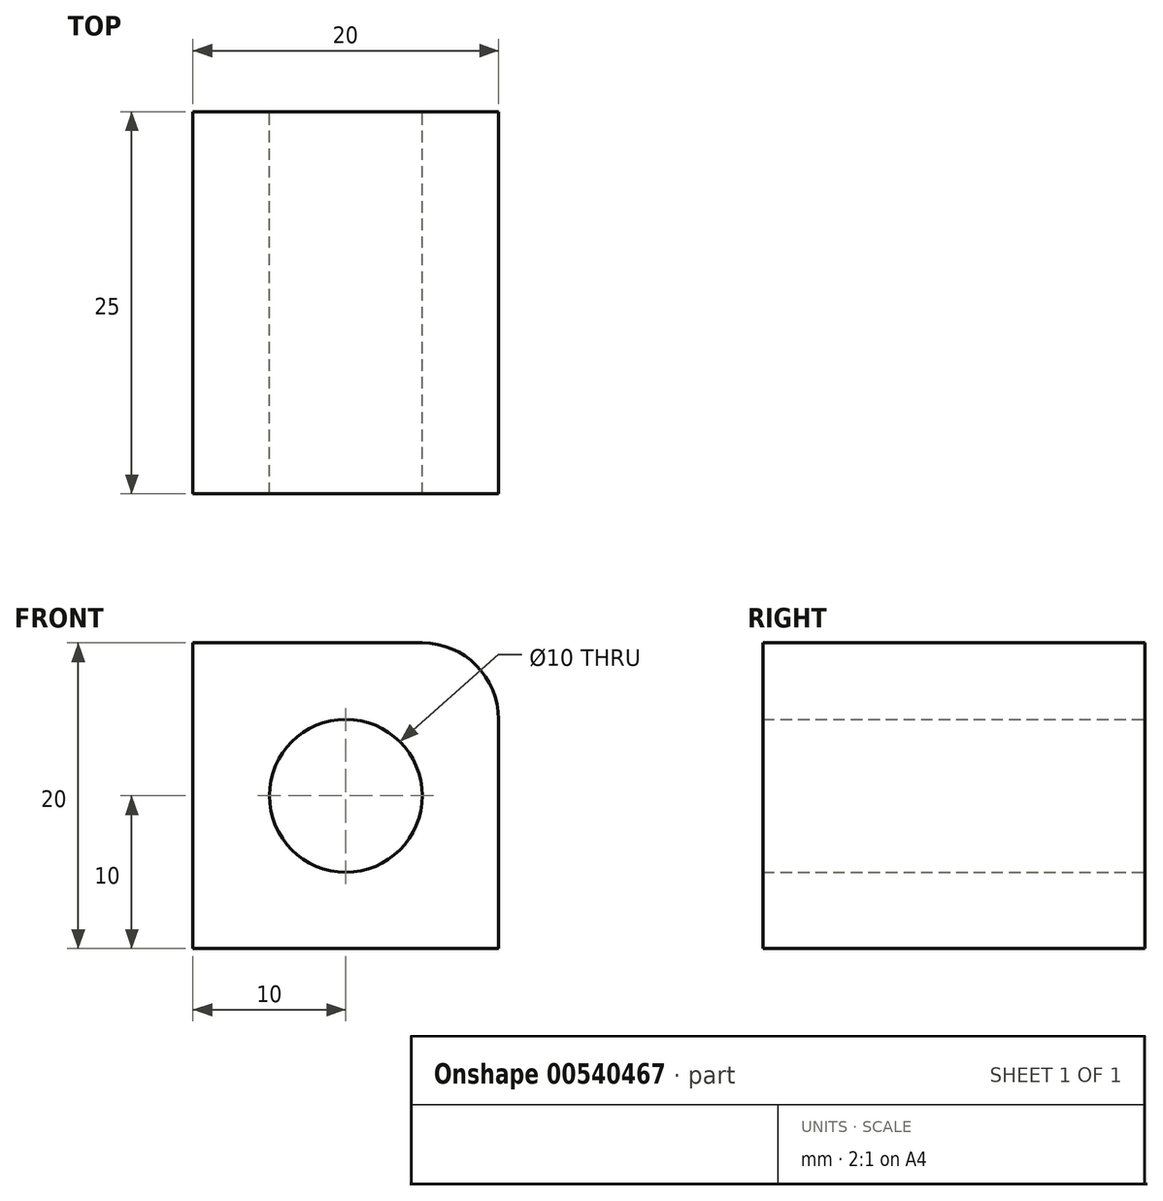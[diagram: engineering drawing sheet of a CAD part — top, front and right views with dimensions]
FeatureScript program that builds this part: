
annotation { "Feature Type Name" : "Feature", "Feature Type Description" : "" }
export const myFeature = defineFeature(function(context is Context, id is Id, definition is map)
    precondition{}
    {
        {
            var Q0;
            Q0=qCreatedBy(makeId("Front.planeOp"),FACE);
            var sketch = newSketch(context, id + "F0", { "sketchPlane" : qUnion([Q0])});
            skLineSegment(sketch, "E0.bottom", {"start": v(-10, 10) * mm, "end": v(5, 10) * mm});
            skLineSegment(sketch, "E0.top", {"start": v(-10, -10) * mm, "end": v(10, -10) * mm});
            skLineSegment(sketch, "E0.left", {"start": v(-10, 10) * mm, "end": v(-10, -10) * mm});
            skLineSegment(sketch, "E0.right", {"start": v(10, 5) * mm, "end": v(10, -10) * mm});
            skPoint(sketch, "E0.middle", {"position": v(0, 0) * mm});
            skPoint(sketch, "E1.visualSharp", {"position": v(10, 10) * mm});
            skArc(sketch, "E1.filletArc", {"start": v(10, 5) * mm, "mid": v(8.54, 8.54) * mm, "end": v(5, 10) * mm});
            skCircle(sketch, "E2", {"center": v(0, 0) * mm, "radius": 5 * mm});
            skSolve(sketch);
        }
        {
            var Q0;
            Q0=makeQuery(id+"F0.imprint","IMPRINT",FACE,{"disambiguationData":[TD([[makeQuery(id+"F0.imprint","IMPRINT",EDGE,{"derivedFrom":sQuery(id+"F0.wireOp",EDGE,"E0.bottom")}),-1.0]])]});
            extrude(context, id + "F1", {"entities" : qUnion([Q0]), "depth" : 25 * mm, "offsetDistance" : 25 * mm});
        }
    });
